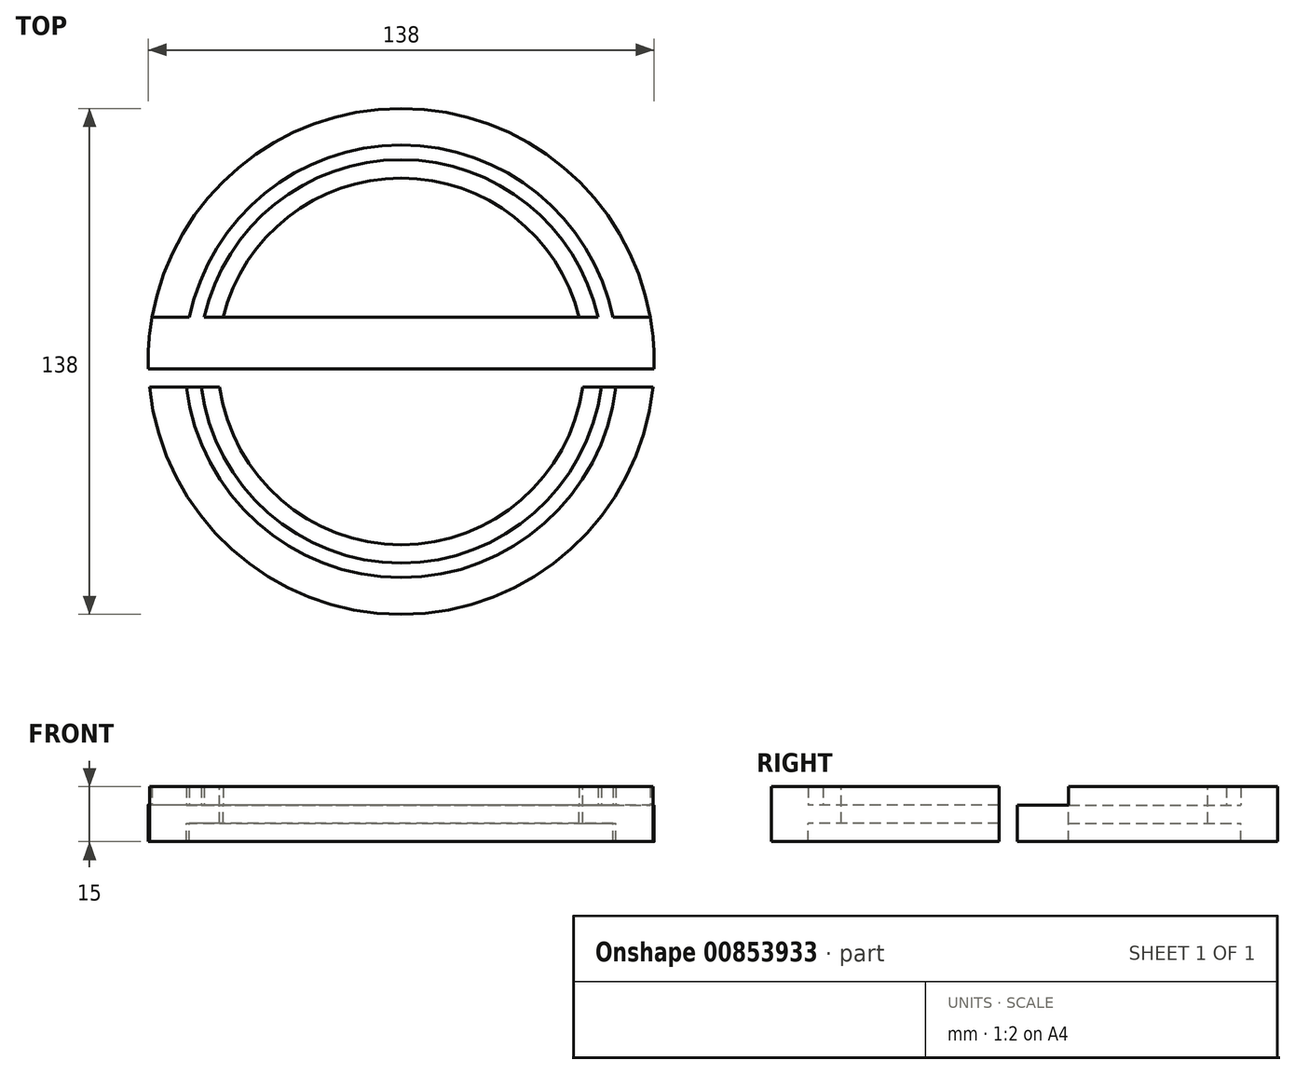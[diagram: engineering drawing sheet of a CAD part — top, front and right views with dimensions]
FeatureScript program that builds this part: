
annotation { "Feature Type Name" : "Feature", "Feature Type Description" : "" }
export const myFeature = defineFeature(function(context is Context, id is Id, definition is map)
    precondition{}
    {
        {
            var Q0;
            Q0=qCreatedBy(makeId("Top.planeOp"),FACE);
            var sketch = newSketch(context, id + "F0", { "sketchPlane" : qUnion([Q0])});
            skArc(sketch, "E0", {"start": v(48.54, 12) * mm, "mid": v(0, 50) * mm, "end": v(-48.54, 12) * mm});
            skCircle(sketch, "E1", {"center": v(0, 0) * mm, "radius": 69 * mm});
            skLineSegment(sketch, "E2", {"start": v(0, 0) * mm, "end": v(0, 2) * mm});
            skLineSegment(sketch, "E3", {"start": v(0, 2) * mm, "end": v(0, 12) * mm});
            skLineSegment(sketch, "E4", {"start": v(0, 12) * mm, "end": v(67.95, 12) * mm});
            skLineSegment(sketch, "E5", {"start": v(0, 0) * mm, "end": v(0, -7) * mm});
            skLineSegment(sketch, "E6", {"start": v(0, -7) * mm, "end": v(68.64, -7) * mm});
            skLineSegment(sketch, "E7", {"start": v(0, 2) * mm, "end": v(68.97, 2) * mm});
            skLineSegment(sketch, "E8", {"start": v(0, 0) * mm, "end": v(0, -2) * mm});
            skLineSegment(sketch, "E9", {"start": v(0, -2) * mm, "end": v(68.97, -2) * mm});
            skLineSegment(sketch, "E10", {"start": v(0, 2) * mm, "end": v(-68.97, 2) * mm});
            skLineSegment(sketch, "E11", {"start": v(0, -2) * mm, "end": v(-68.97, -2) * mm});
            skLineSegment(sketch, "E12", {"start": v(0, 12) * mm, "end": v(-67.95, 12) * mm});
            skLineSegment(sketch, "E13", {"start": v(0, -7) * mm, "end": v(-68.64, -7) * mm});
            skArc(sketch, "E14.trimOffspring", {"start": v(53.67, 12) * mm, "mid": v(0, 55) * mm, "end": v(-53.67, 12) * mm});
            skArc(sketch, "E15.trimOffspring", {"start": v(57.77, 12) * mm, "mid": v(0, 59) * mm, "end": v(-57.77, 12) * mm});
            skArc(sketch, "E16.trimOffspring", {"start": v(-54.55, -7) * mm, "mid": v(0, -55) * mm, "end": v(54.55, -7) * mm});
            skArc(sketch, "E17.trimOffspring", {"start": v(-58.58, -7) * mm, "mid": v(0, -59) * mm, "end": v(58.58, -7) * mm});
            skArc(sketch, "E18.trimOffspring", {"start": v(-49.5, -7) * mm, "mid": v(0, -50) * mm, "end": v(49.5, -7) * mm});
            skSolve(sketch);
        }
        {
            var Q0;
            {var subQ5=sQuery(id+"F0.wireOp",EDGE,"E3");Q0=makeQuery(id+"F0.imprint","IMPRINT",FACE,{"disambiguationData":[TD([[makeQuery(id+"F0.imprint","IMPRINT",EDGE,{"derivedFrom":subQ5}),1.0]])]});}
            var Q1;
            {var subQ0=sQuery(id+"F0.wireOp",EDGE,"E12");var subQ1=sQuery(id+"F0.wireOp",EDGE,"tg0MKUt5-zvSe-tF1P-xDEn-VmMZgnL0rZEm");var subQ2=makeQuery(id+"F0.imprint","INTERSECT",VERTEX,{"derivedFrom":[subQ1,subQ0]});Q1=makeQuery(id+"F0.imprint","IMPRINT",FACE,{"disambiguationData":[TD([[makeQuery(id+"F0.imprint","IMPRINT",EDGE,{"disambiguationData":[TD([[subQ2,-1.0]])],"derivedFrom":subQ1}),-1.0]])]});}
            var Q2;
            {var subQ0=sQuery(id+"F0.wireOp",EDGE,"E12");var subQ1=sQuery(id+"F0.wireOp",EDGE,"ryH7h19n-vrf8-8470-h2Tu-mjXFAZmi1gBa");var subQ2=makeQuery(id+"F0.imprint","INTERSECT",VERTEX,{"derivedFrom":[subQ1,subQ0]});Q2=makeQuery(id+"F0.imprint","IMPRINT",FACE,{"disambiguationData":[TD([[makeQuery(id+"F0.imprint","IMPRINT",EDGE,{"disambiguationData":[TD([[subQ2,-1.0]])],"derivedFrom":subQ1}),-1.0]])]});}
            var Q3;
            {var subQ0=sQuery(id+"F0.wireOp",EDGE,"E10");var subQ1=sQuery(id+"F0.wireOp",EDGE,"ryH7h19n-vrf8-8470-h2Tu-mjXFAZmi1gBa");var subQ2=makeQuery(id+"F0.imprint","INTERSECT",VERTEX,{"derivedFrom":[subQ1,subQ0]});Q3=makeQuery(id+"F0.imprint","IMPRINT",FACE,{"disambiguationData":[TD([[makeQuery(id+"F0.imprint","IMPRINT",EDGE,{"disambiguationData":[TD([[subQ2,-1.0]])],"derivedFrom":subQ1}),-1.0]])]});}
            var Q4;
            {var subQ0=sQuery(id+"F0.wireOp",EDGE,"E10");var subQ1=sQuery(id+"F0.wireOp",EDGE,"tg0MKUt5-zvSe-tF1P-xDEn-VmMZgnL0rZEm");var subQ2=makeQuery(id+"F0.imprint","INTERSECT",VERTEX,{"derivedFrom":[subQ1,subQ0]});Q4=makeQuery(id+"F0.imprint","IMPRINT",FACE,{"disambiguationData":[TD([[makeQuery(id+"F0.imprint","IMPRINT",EDGE,{"disambiguationData":[TD([[subQ2,-1.0]])],"derivedFrom":subQ1}),-1.0]])]});}
            var Q5;
            {var subQ0=sQuery(id+"F0.wireOp",EDGE,"E11");var subQ1=sQuery(id+"F0.wireOp",EDGE,"tg0MKUt5-zvSe-tF1P-xDEn-VmMZgnL0rZEm");var subQ2=makeQuery(id+"F0.imprint","INTERSECT",VERTEX,{"derivedFrom":[subQ1,subQ0]});Q5=makeQuery(id+"F0.imprint","IMPRINT",FACE,{"disambiguationData":[TD([[makeQuery(id+"F0.imprint","IMPRINT",EDGE,{"disambiguationData":[TD([[subQ2,-1.0]])],"derivedFrom":subQ1}),-1.0]])]});}
            var Q6;
            {var subQ0=sQuery(id+"F0.wireOp",EDGE,"E11");var subQ1=sQuery(id+"F0.wireOp",EDGE,"ryH7h19n-vrf8-8470-h2Tu-mjXFAZmi1gBa");var subQ2=makeQuery(id+"F0.imprint","INTERSECT",VERTEX,{"derivedFrom":[subQ1,subQ0]});Q6=makeQuery(id+"F0.imprint","IMPRINT",FACE,{"disambiguationData":[TD([[makeQuery(id+"F0.imprint","IMPRINT",EDGE,{"disambiguationData":[TD([[subQ2,-1.0]])],"derivedFrom":subQ1}),-1.0]])]});}
            var Q7;
            {var subQ5=sQuery(id+"F0.wireOp",EDGE,"E5");Q7=makeQuery(id+"F0.imprint","IMPRINT",FACE,{"disambiguationData":[TD([[makeQuery(id+"F0.imprint","IMPRINT",EDGE,{"derivedFrom":subQ5}),-1.0]])]});}
            var Q8;
            {var subQ5=sQuery(id+"F0.wireOp",EDGE,"E5");Q8=makeQuery(id+"F0.imprint","IMPRINT",FACE,{"disambiguationData":[TD([[makeQuery(id+"F0.imprint","IMPRINT",EDGE,{"derivedFrom":subQ5}),1.0]])]});}
            var Q9;
            {var subQ1=sQuery(id+"F0.wireOp",EDGE,"E2");Q9=makeQuery(id+"F0.imprint","IMPRINT",FACE,{"disambiguationData":[TD([[makeQuery(id+"F0.imprint","IMPRINT",EDGE,{"derivedFrom":subQ1}),-1.0]])]});}
            var Q10;
            {var subQ5=sQuery(id+"F0.wireOp",EDGE,"E3");Q10=makeQuery(id+"F0.imprint","IMPRINT",FACE,{"disambiguationData":[TD([[makeQuery(id+"F0.imprint","IMPRINT",EDGE,{"derivedFrom":subQ5}),-1.0]])]});}
            var Q11;
            {var subQ0=sQuery(id+"F0.wireOp",EDGE,"E7");var subQ3=sQuery(id+"F0.wireOp",EDGE,"tg0MKUt5-zvSe-tF1P-xDEn-VmMZgnL0rZEm");var subQ4=makeQuery(id+"F0.imprint","INTERSECT",VERTEX,{"derivedFrom":[subQ3,subQ0]});Q11=makeQuery(id+"F0.imprint","IMPRINT",FACE,{"disambiguationData":[TD([[makeQuery(id+"F0.imprint","IMPRINT",EDGE,{"disambiguationData":[TD([[subQ4,1.0]])],"derivedFrom":subQ3}),1.0]])]});}
            var Q12;
            {var subQ2=sQuery(id+"F0.wireOp",EDGE,"E3");Q12=makeQuery(id+"F0.imprint","IMPRINT",FACE,{"disambiguationData":[TD([[makeQuery(id+"F0.imprint","IMPRINT",EDGE,{"derivedFrom":subQ2}),1.0]])]});}
            var Q13;
            Q13=makeQuery(id+"F0.imprint","IMPRINT",FACE,{"disambiguationData":[TD([[makeQuery(id+"F0.imprint","IMPRINT",EDGE,{"derivedFrom":sQuery(id+"F0.wireOp",EDGE,"E2")}),1.0]])]});
            extrude(context, id + "F1", {"entities" : qUnion([Q0, Q1, Q2, Q3, Q4, Q5, Q6, Q7, Q8, Q9, Q10, Q11, Q12, Q13]), "oppositeDirection" : true, "depth" : 10 * mm, "offsetDistance" : 25 * mm, "hasSecondDirection" : true, "secondDirectionOppositeDirection" : true, "secondDirectionDepth" : 5 * mm});
        }
        {
            var Q0;
            {var subQ1=sQuery(id+"F0.wireOp",EDGE,"E5");Q0=makeQuery(id+"F0.imprint","IMPRINT",FACE,{"disambiguationData":[TD([[makeQuery(id+"F0.imprint","IMPRINT",EDGE,{"derivedFrom":subQ1}),-1.0]])]});}
            var Q1;
            {var subQ2=sQuery(id+"F0.wireOp",EDGE,"E3");Q1=makeQuery(id+"F0.imprint","IMPRINT",FACE,{"disambiguationData":[TD([[makeQuery(id+"F0.imprint","IMPRINT",EDGE,{"derivedFrom":subQ2}),1.0]])]});}
            var Q2;
            {var subQ6=sQuery(id+"F0.wireOp",EDGE,"E3");Q2=makeQuery(id+"F0.imprint","IMPRINT",FACE,{"disambiguationData":[TD([[makeQuery(id+"F0.imprint","IMPRINT",EDGE,{"derivedFrom":subQ6}),-1.0]])]});}
            var Q3;
            {var subQ1=sQuery(id+"F0.wireOp",EDGE,"E5");Q3=makeQuery(id+"F0.imprint","IMPRINT",FACE,{"disambiguationData":[TD([[makeQuery(id+"F0.imprint","IMPRINT",EDGE,{"derivedFrom":subQ1}),1.0]])]});}
            extrude(context, id + "F2", {"entities" : qUnion([Q0, Q1, Q2, Q3]), "operationType" : NewBodyOperationType.ADD, "oppositeDirection" : true, "depth" : 5 * mm, "offsetDistance" : 25 * mm});
        }
        {
            var Q0;
            {var subQ5=sQuery(id+"F0.wireOp",EDGE,"E15.trimOffspring");Q0=makeQuery(id+"F0.imprint","IMPRINT",FACE,{"disambiguationData":[TD([[makeQuery(id+"F0.imprint","IMPRINT",EDGE,{"derivedFrom":subQ5}),-1.0]])]});}
            var Q1;
            {var subQ5=sQuery(id+"F0.wireOp",EDGE,"E17.trimOffspring");Q1=makeQuery(id+"F0.imprint","IMPRINT",FACE,{"disambiguationData":[TD([[makeQuery(id+"F0.imprint","IMPRINT",EDGE,{"derivedFrom":subQ5}),-1.0]])]});}
            extrude(context, id + "F3", {"entities" : qUnion([Q0, Q1]), "operationType" : NewBodyOperationType.ADD, "oppositeDirection" : true, "depth" : 10 * mm, "offsetDistance" : 25 * mm});
        }
        {
            var Q0;
            {var subQ0=sQuery(id+"F0.wireOp",EDGE,"E16.trimOffspring");Q0=makeQuery(id+"F0.imprint","IMPRINT",FACE,{"disambiguationData":[TD([[makeQuery(id+"F0.imprint","IMPRINT",EDGE,{"derivedFrom":subQ0}),1.0]])]});}
            var Q1;
            {var subQ0=sQuery(id+"F0.wireOp",EDGE,"E0");Q1=makeQuery(id+"F0.imprint","IMPRINT",FACE,{"disambiguationData":[TD([[makeQuery(id+"F0.imprint","IMPRINT",EDGE,{"derivedFrom":subQ0}),-1.0]])]});}
            var Q2;
            {var subQ0=sQuery(id+"F0.wireOp",EDGE,"E14.trimOffspring");Q2=makeQuery(id+"F0.imprint","IMPRINT",FACE,{"disambiguationData":[TD([[makeQuery(id+"F0.imprint","IMPRINT",EDGE,{"derivedFrom":subQ0}),-1.0]])]});}
            var Q3;
            {var subQ0=sQuery(id+"F0.wireOp",EDGE,"E16.trimOffspring");Q3=makeQuery(id+"F0.imprint","IMPRINT",FACE,{"disambiguationData":[TD([[makeQuery(id+"F0.imprint","IMPRINT",EDGE,{"derivedFrom":subQ0}),-1.0]])]});}
            extrude(context, id + "F4", {"entities" : qUnion([Q0, Q1, Q2, Q3]), "operationType" : NewBodyOperationType.ADD, "oppositeDirection" : true, "depth" : 5 * mm, "offsetDistance" : 25 * mm});
        }
        {
            var Q0;
            {var subQ5=sQuery(id+"F0.wireOp",EDGE,"E15.trimOffspring");Q0=makeQuery(id+"F0.imprint","IMPRINT",FACE,{"disambiguationData":[TD([[makeQuery(id+"F0.imprint","IMPRINT",EDGE,{"derivedFrom":subQ5}),-1.0]])]});}
            var Q1;
            {var subQ0=sQuery(id+"F0.wireOp",EDGE,"E0");Q1=makeQuery(id+"F0.imprint","IMPRINT",FACE,{"disambiguationData":[TD([[makeQuery(id+"F0.imprint","IMPRINT",EDGE,{"derivedFrom":subQ0}),-1.0]])]});}
            var Q2;
            {var subQ5=sQuery(id+"F0.wireOp",EDGE,"E17.trimOffspring");Q2=makeQuery(id+"F0.imprint","IMPRINT",FACE,{"disambiguationData":[TD([[makeQuery(id+"F0.imprint","IMPRINT",EDGE,{"derivedFrom":subQ5}),-1.0]])]});}
            var Q3;
            {var subQ0=sQuery(id+"F0.wireOp",EDGE,"E16.trimOffspring");Q3=makeQuery(id+"F0.imprint","IMPRINT",FACE,{"disambiguationData":[TD([[makeQuery(id+"F0.imprint","IMPRINT",EDGE,{"derivedFrom":subQ0}),1.0]])]});}
            extrude(context, id + "F5", {"entities" : qUnion([Q0, Q1, Q2, Q3]), "operationType" : NewBodyOperationType.ADD, "depth" : 5 * mm, "offsetDistance" : 25 * mm});
        }
    });
